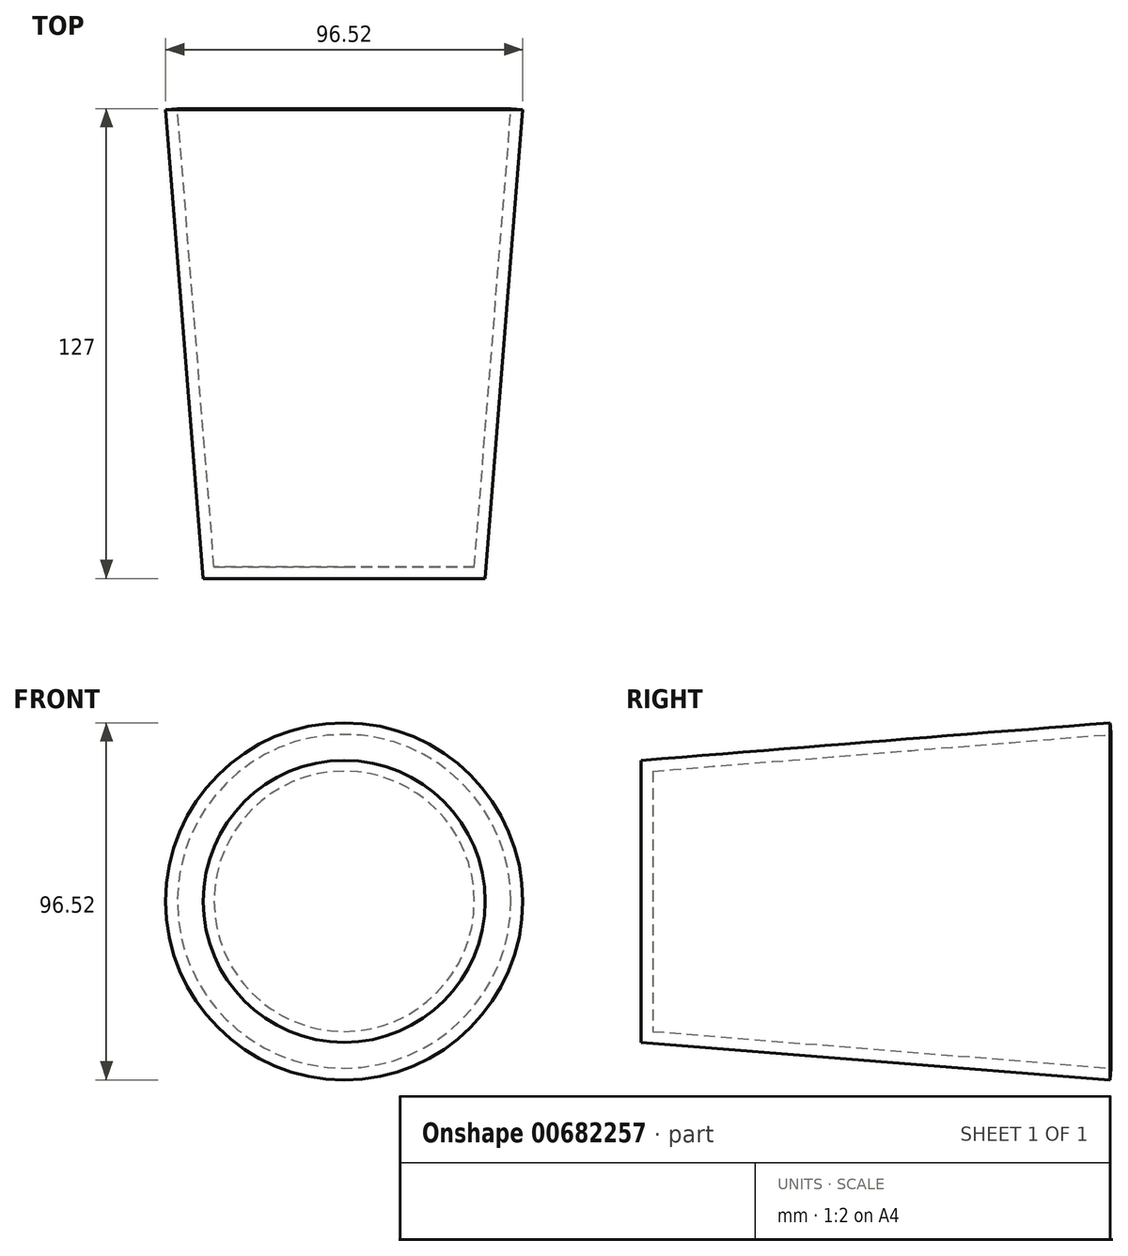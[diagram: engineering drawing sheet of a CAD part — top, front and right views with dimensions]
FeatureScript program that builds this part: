
annotation { "Feature Type Name" : "Feature", "Feature Type Description" : "" }
export const myFeature = defineFeature(function(context is Context, id is Id, definition is map)
    precondition{}
    {
        {
            var Q0;
            Q0=qCreatedBy(makeId("Top.planeOp"),FACE);
            var sketch = newSketch(context, id + "F0", { "sketchPlane" : qUnion([Q0])});
            skLineSegment(sketch, "E0", {"start": v(0, 0) * mm, "end": v(-38.1, 0) * mm});
            skLineSegment(sketch, "E1", {"start": v(-38.1, 0) * mm, "end": v(-48.26, 126.75) * mm});
            skLineSegment(sketch, "E2", {"start": v(-48.26, 126.75) * mm, "end": v(-45.1, 127) * mm});
            skLineSegment(sketch, "E3", {"start": v(-45.1, 127) * mm, "end": v(-35.17, 3.17) * mm});
            skLineSegment(sketch, "E4", {"start": v(-35.17, 3.17) * mm, "end": v(0, 3.17) * mm});
            skLineSegment(sketch, "E5", {"start": v(0, 3.17) * mm, "end": v(0, 0) * mm});
            skSolve(sketch);
        }
        {
            var Q0;
            Q0=makeQuery(id+"F0.imprint","IMPRINT",FACE,{"disambiguationData":[TD([[makeQuery(id+"F0.imprint","IMPRINT",EDGE,{"derivedFrom":sQuery(id+"F0.wireOp",EDGE,"E0")}),-1.0]])]});
            var Q1;
            Q1=sQuery(id+"F0.wireOp",EDGE,"E5");
            revolve(context, id + "F1", {"entities" : qUnion([Q0]), "axis" : qUnion([Q1]), "revolveType" : RevolveType.FULL});
        }
    });
